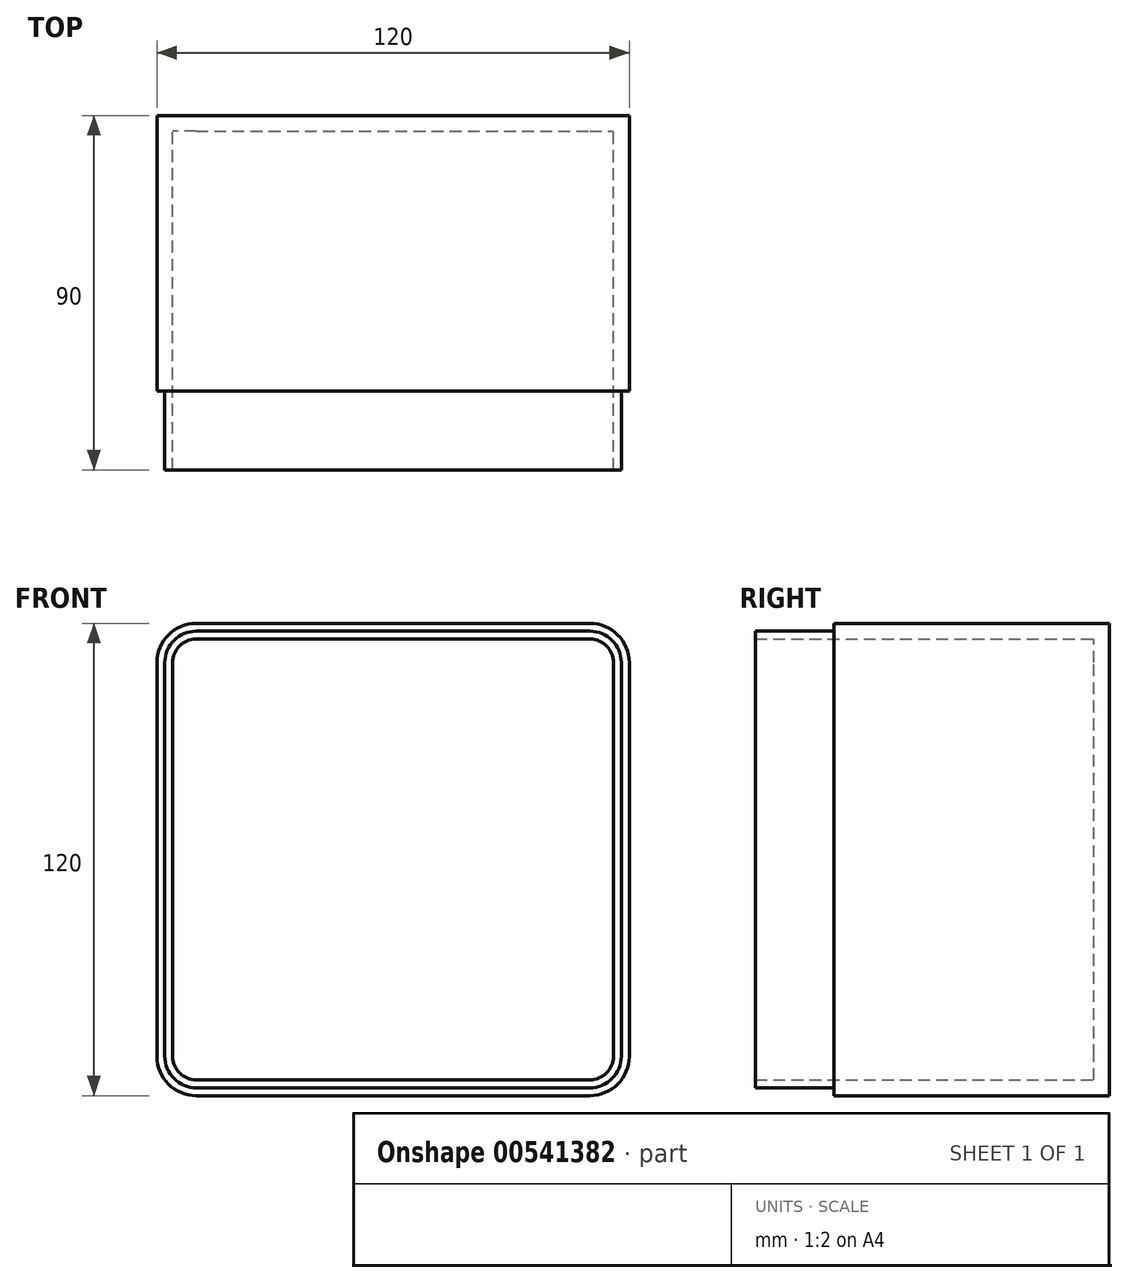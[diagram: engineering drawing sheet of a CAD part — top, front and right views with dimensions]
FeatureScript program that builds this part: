
annotation { "Feature Type Name" : "Feature", "Feature Type Description" : "" }
export const myFeature = defineFeature(function(context is Context, id is Id, definition is map)
    precondition{}
    {
        {
            var Q0;
            Q0=qCreatedBy(makeId("Front.planeOp"),FACE);
            var sketch = newSketch(context, id + "F0", { "sketchPlane" : qUnion([Q0])});
            skLineSegment(sketch, "E0.bottom", {"start": v(0, 0) * mm, "end": v(120, 0) * mm});
            skLineSegment(sketch, "E0.top", {"start": v(0, 120) * mm, "end": v(120, 120) * mm});
            skLineSegment(sketch, "E0.left", {"start": v(0, 0) * mm, "end": v(0, 120) * mm});
            skLineSegment(sketch, "E0.right", {"start": v(120, 0) * mm, "end": v(120, 120) * mm});
            skSolve(sketch);
        }
        {
            var Q0;
            Q0=makeQuery(id+"F0.imprint","IMPRINT",FACE,{"disambiguationData":[TD([[makeQuery(id+"F0.imprint","IMPRINT",EDGE,{"derivedFrom":sQuery(id+"F0.wireOp",EDGE,"E0.bottom")}),1.0]])]});
            extrude(context, id + "F1", {"entities" : qUnion([Q0]), "depth" : 90 * mm, "offsetDistance" : 25.4 * mm});
        }
        {
            var Q0;
            Q0=makeQuery(id+"F1.opExtrude","SWEPT_EDGE",EDGE,{"disambiguationData":[OSD([sQuery(id+"F0.wireOp",EDGE,"E0.top"),sQuery(id+"F0.wireOp",EDGE,"E0.left")])]});
            var Q1;
            Q1=makeQuery(id+"F1.opExtrude","SWEPT_EDGE",EDGE,{"disambiguationData":[OSD([sQuery(id+"F0.wireOp",EDGE,"E0.top"),sQuery(id+"F0.wireOp",EDGE,"E0.right")])]});
            var Q2;
            Q2=makeQuery(id+"F1.opExtrude","SWEPT_EDGE",EDGE,{"disambiguationData":[OSD([sQuery(id+"F0.wireOp",EDGE,"E0.bottom"),sQuery(id+"F0.wireOp",EDGE,"E0.right")])]});
            var Q3;
            Q3=makeQuery(id+"F1.opExtrude","SWEPT_EDGE",EDGE,{"disambiguationData":[OSD([sQuery(id+"F0.wireOp",EDGE,"E0.bottom"),sQuery(id+"F0.wireOp",EDGE,"E0.left")])]});
            fillet(context, id + "F2", {"entities" : qUnion([Q0, Q1, Q2, Q3]), "radius" : 10 * mm, "tangentPropagation" : true, "allowEdgeOverflow" : false});
        }
        {
            var Q0;
            Q0=makeQuery(id+"F1.opExtrude","CAP_FACE",FACE,{"disambiguationData":[OSD([sQuery(id+"F0.wireOp",EDGE,"E0.bottom"),sQuery(id+"F0.wireOp",EDGE,"E0.top"),sQuery(id+"F0.wireOp",EDGE,"E0.left"),sQuery(id+"F0.wireOp",EDGE,"E0.right")])],"isStart":false});
            shell(context, id + "F3", {"entities" : qUnion([Q0]), "thickness" : 4 * mm});
        }
        {
            var Q0;
            Q0=makeQuery(id+"F1.opExtrude","CAP_FACE",FACE,{"disambiguationData":[OSD([sQuery(id+"F0.wireOp",EDGE,"E0.bottom"),sQuery(id+"F0.wireOp",EDGE,"E0.top"),sQuery(id+"F0.wireOp",EDGE,"E0.left"),sQuery(id+"F0.wireOp",EDGE,"E0.right")])],"isStart":false});
            var sketch = newSketch(context, id + "F4", { "sketchPlane" : qUnion([Q0])});
            skLineSegment(sketch, "E1.0", {"start": v(10, 118) * mm, "end": v(110, 118) * mm});
            skArc(sketch, "E1.1", {"start": v(118, 110) * mm, "mid": v(115.66, 115.66) * mm, "end": v(110, 118) * mm});
            skArc(sketch, "E1.2", {"start": v(10, 118) * mm, "mid": v(4.34, 115.66) * mm, "end": v(2, 110) * mm});
            skLineSegment(sketch, "E1.3", {"start": v(118, 10) * mm, "end": v(118, 110) * mm});
            skLineSegment(sketch, "E1.4", {"start": v(2, 10) * mm, "end": v(2, 110) * mm});
            skArc(sketch, "E1.5", {"start": v(2, 10) * mm, "mid": v(4.34, 4.34) * mm, "end": v(10, 2) * mm});
            skLineSegment(sketch, "E1.6", {"start": v(10, 2) * mm, "end": v(110, 2) * mm});
            skArc(sketch, "E1.7", {"start": v(110, 2) * mm, "mid": v(115.66, 4.34) * mm, "end": v(118, 10) * mm});
            skSolve(sketch);
        }
        {
            var Q0;
            Q0=makeQuery(id+"F4.imprint","IMPRINT",FACE,{"disambiguationData":[TD([[makeQuery(id+"F4.imprint","IMPRINT",EDGE,{"derivedFrom":sQuery(id+"F4.wireOp",EDGE,"E1.0")}),1.0]])]});
            extrude(context, id + "F5", {"entities" : qUnion([Q0]), "operationType" : NewBodyOperationType.REMOVE, "oppositeDirection" : true, "depth" : 20 * mm, "offsetDistance" : 25.4 * mm});
        }
    });
